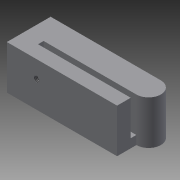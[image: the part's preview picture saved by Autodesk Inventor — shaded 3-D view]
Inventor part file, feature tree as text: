
AUTODESK INVENTOR PART (.ipt)
format: ipt  version: 2014 (Build 180170000, 170)  size: 124,416 bytes
history: native  units: mm
features: sketch x6, extrude x5, fillet x1, hole x1, projected_geometry x1
ambient origin geometry x8: Origin, YZ Plane, XZ Plane, XY Plane, X Axis, Y Axis, Z Axis, Center Point
bodies: Body1 (feature_tree)
feature tree (14):
  extrude  "Extrusion7"  Depth=25.0mm
  extrude  "Extrusion8"  Depth=10.0mm
  extrude  "Extrusion9"  Depth=14.0mm
  fillet  "Rundung4"  Radius=14.0mm
  extrude  "Extrusion10"  Depth=7.0mm
  hole  "Bohrung1"  [1 undecoded]
  extrude  "Extrusion11"  Depth=5.0mm
  sketch  "Skizze8"  dims[d28=62.931mm d29=25.0mm]
  sketch  "Skizze9"  dims[d30=5.0mm d31=0.0mm d32=10.0mm]
  sketch  "Skizze10"  dims[d33=20.0mm d34=0.0mm d35=59.931mm d36=14.0mm]
  sketch  "Skizze11"  dims[d37=20.0mm d38=0.0mm d39=7.0mm]
  sketch  "Skizze12"  dims[d40=7.8mm d41=20.0mm d42=0.0mm]
  sketch  "Skizze13"  dims[d43=7.0mm d44=9.9mm d45=3.242mm d46=18.0mm d47=3.023mm d48=2.0mm d49=14.3117mm d50=20.0mm d51=20.594885mm d52=5.0mm d53=0.0mm]
  projected_geometry  "Projizierte Kontur1"
note: 1 required parameter value undecoded (feature->parameter linkage not recoverable at this tier; creation-order binding heuristic only, values carry confidence <= 0.55)
